# Revit family: Faucet-Electronic_No_Touch-Sloan-Basys-EFX-1XX.X0X.0XXX
name_source: partatom
category: Plumbing Fixtures
revit_build: Autodesk Revit 2014 (Build: 20130308_1515(x64)
units: mm (PartAtom-declared; Revit-internal decimal feet)

## types (7) — shared parameters
ADA Compliant = Yes
Assembly Code = D2020
CP- Chrome Plated Finish = Yes
CW Connection = Yes
CWFU = 1.5
Default Elevation = 48"
Description = Battery powered, sensor activated, electronic, chrome plated die cast body, hand washing faucet for pre-tempered or hot and cold water operation.
EAF-17-A = 126" Extension Cable
EAF-23 = Splitter
EAF-24-A = 11-13/16" Extension Cable
EAF-25-A = 47-1/4" Extension Cable
Faucet Body = Zinc Die Cast
Faucet Height = 10"
HWFU = 1.5
Low Lead California Health and Safety Code 116875 (AB1953-2006) = Yes
Manufacturer = Sloan Valve Company
Mounting = Single Hole Deck
Operation = Sensor
PVDSF- PVD Satin (Chrome) Finish = Yes
Product Documentation Link = http://www.sloanvalve.com
Product URL = http://www.sloanvalve.com
Solar + LCD Display Crown = No
Standard Crown = No
Vent Connection = No
Vermont Bill S.152 = Yes
WFU = 2
Warranty = 3 Year (limited)
Waste Connection = No
cUPC (ASME A112.18.1M/CSA B125.1) = Yes

## per-type parameters (varying)
| type | HW Connection | ISM | Integral Side Mixer | Model | Solar Crown | URL | Visible | Visible 2 | Visible 3 | Visible 4 | Visible 5 | Visible 6 | Visible 7 | plate |
| EFX-1XX Series | No | 3 1/8" | No | EFX-1XX Series | No | http://www.sloanvalve.com | No | Yes | No | No | No | Yes | No | 6" |
| EFX-1XX-5 Series | No | 1/8" | Yes | EFX-1XX Series | No | www.atsspec.ca | No | Yes | No | Yes | No | Yes | No | 6" |
| EFX-1XX Series-4in | No | 3 1/8" | No | EFX-1XX Series | No | www.atsspec.ca | No | No | Yes | No | Yes | No | Yes | 6" |
| EFX-1XX-5 Series-4in | No | 1/8" | Yes | EFX-1XX Series | No | www.atsspec.ca | Yes | No | No | No | Yes | No | Yes | 6" |
| EFX-1XX Series-8in | No | 3 1/8" | No | EFX-1XX Series | No | www.atsspec.ca | No | No | Yes | No | Yes | No | Yes | 8" |
| EFX-1XX-5 Series-8in | No | 1/8" | Yes | EFX-1XX Series | No | www.atsspec.ca | Yes | No | No | No | Yes | No | Yes | 8" |
| EFX-17X-5 Series-8in | Yes | 1/8" | Yes | EFX-17X-5 Series-8in | Yes | http://www.sloanvalve.com | Yes | No | No | No | Yes | No | Yes | 8" |

## geometry (parser evidence)
native form markers: Sweep x1
no freeform markers — native parametric forms only
